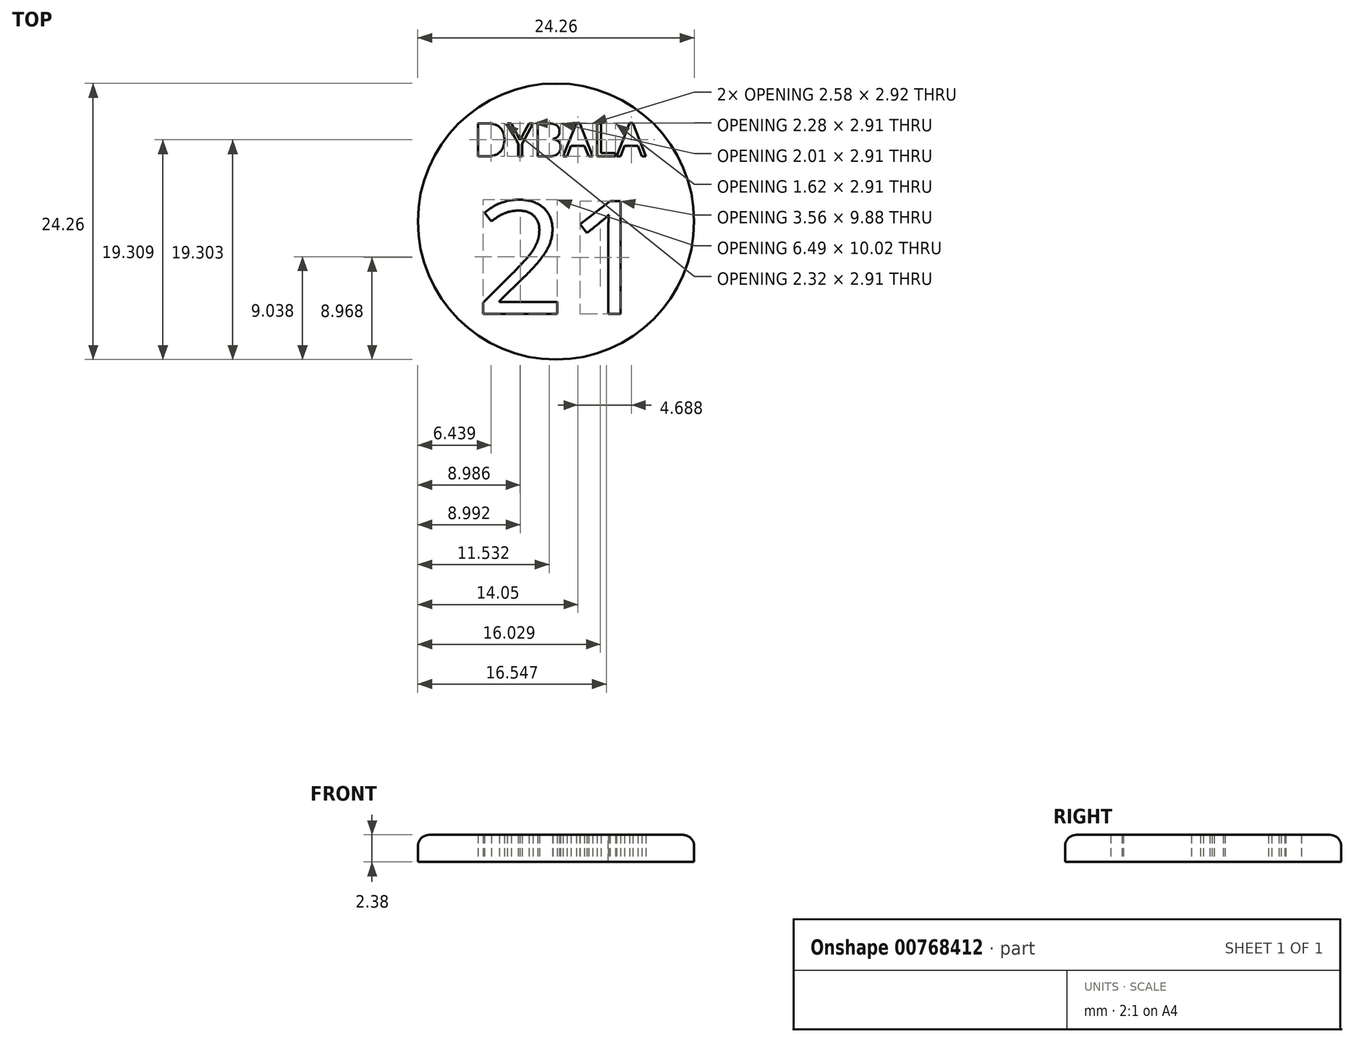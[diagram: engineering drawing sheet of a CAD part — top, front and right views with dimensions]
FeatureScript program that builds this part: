
annotation { "Feature Type Name" : "Feature", "Feature Type Description" : "" }
export const myFeature = defineFeature(function(context is Context, id is Id, definition is map)
    precondition{}
    {
        {
            var Q0;
            Q0=qCreatedBy(makeId("Top.planeOp"),FACE);
            var sketch = newSketch(context, id + "F0", { "sketchPlane" : qUnion([Q0])});
            skCircle(sketch, "E0", {"center": v(0, 0) * mm, "radius": 12.12 * mm});
            skText(sketch, "E1", { "text": "DYBALA", "fontName": "OpenSans-Regular.ttf"});
            skText(sketch, "E2", { "text": "21", "fontName": "OpenSans-Regular.ttf"});
            const initialGuessF0  = {"E1": [-0.00725, 0.00572, 1, 0, 0.00293], "E2": [-0.00706, -0.0081, 1, 0, 0.00996]};
            skSetInitialGuess(sketch, initialGuessF0);
            skSolve(sketch);
        }
        {
            var Q0;
            Q0=makeQuery(id+"F0.imprint","IMPRINT",FACE,{"disambiguationData":[TD([[makeQuery(id+"F0.imprint","IMPRINT",EDGE,{"derivedFrom":sQuery(id+"F0.wireOp",EDGE,"E0")}),1.0]])]});
            extrude(context, id + "F1", {"entities" : qUnion([Q0]), "depth" : 2.38 * mm, "offsetDistance" : 25 * mm});
        }
        {
            var Q0;
            Q0=makeQuery(id+"F1.opExtrude","CAP_EDGE",EDGE,{"disambiguationData":[OSD([sQuery(id+"F0.wireOp",EDGE,"E0")])],"isStart":false});
            fillet(context, id + "F2", {"entities" : qUnion([Q0]), "radius" : 1 * mm, "tangentPropagation" : true, "allowEdgeOverflow" : false});
        }
    });
